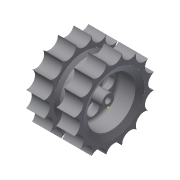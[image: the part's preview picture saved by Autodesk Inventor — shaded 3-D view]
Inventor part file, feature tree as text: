
AUTODESK INVENTOR PART (.ipt)
format: ipt  version: 2015 (Build 190159000, 159)  size: 267,776 bytes
history: native  units: mm
features: sketch x8, hole x4, revolve x1
ambient origin geometry x8: Origin, YZ Plane, XZ Plane, XY Plane, X Axis, Y Axis, Z Axis, Center Point
bodies: Solid1 (feature_tree)
feature tree (13):
  revolve  "Revolution1"  [1 undecoded]
  hole  "Hole1"  [1 undecoded]
  hole  "Hole2"  [1 undecoded]
  sketch  "Sketch4"  dims[d14=90.0deg d15=3.0mm]
  hole  "Hole3"  [1 undecoded]
  sketch  "Sketch6"  dims[d18=3.0mm]
  sketch  "Sketch7"  dims[d19=5.0mm d20=6.0mm d21=4.0mm d22=2.0mm d23=90.0deg d24=8.0mm d25=0.0mm]
  sketch  "Sketch8"  dims[d26=5.0mm d27=5.0mm d29=5.0mm d31=3.0mm d32=3.0mm d33=3.0mm d34=3.0mm d35=4.0mm d36=6.0mm d37=4.0mm d38=2.0mm d39=90.0deg d40=8.0mm d41=0.0mm d42=2.0mm d43=6.0mm d44=4.0mm d45=2.0mm d46=90.0deg d47=20.0mm d48=0.0mm d49=2.0mm d50=1.0mm d51=4.0mm d52=4.0mm d53=6.0mm d54=14.0mm d55=14.0mm d56=14.0mm d57=14.0mm d58=14.0mm d59=45.0deg d60=14.0mm d61=135.0deg d62=14.0mm d63=135.0deg d64=14.0mm d65=14.0mm d66=22.5deg d67=14.0mm d68=14.0mm d69=14.0mm d70=112.5deg d71=14.0mm d72=157.5deg d73=14.0mm d74=157.5deg d75=14.0mm d76=112.5deg d77=5.5mm d78=6.0mm d79=4.0mm d80=2.0mm d81=90.0deg d82=20.0mm d83=0.0mm]
  hole  "Hole4"  [1 undecoded]
  sketch  "Sketch1"  dims[d0=6.0mm d1=2.0mm]
  sketch  "Sketch2"  dims[d3=5.0mm d6=12.0mm]
  sketch  "Sketch3"  dims[d7=2.0mm d8=5.0mm]
  sketch  "Sketch5"  dims[d16=3.0mm d17=3.0mm]
note: 5 required parameter values undecoded (feature->parameter linkage not recoverable at this tier; creation-order binding heuristic only, values carry confidence <= 0.55)